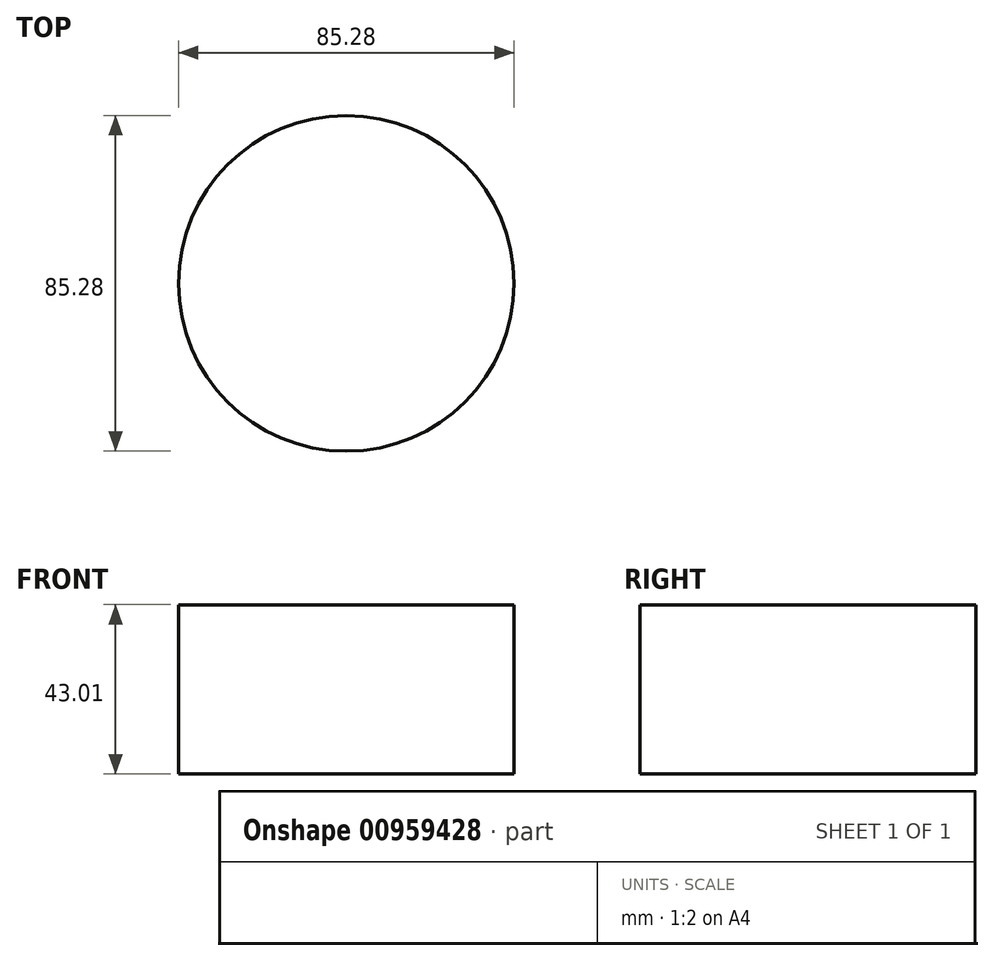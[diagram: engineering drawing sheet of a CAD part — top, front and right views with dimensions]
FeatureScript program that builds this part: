
annotation { "Feature Type Name" : "Feature", "Feature Type Description" : "" }
export const myFeature = defineFeature(function(context is Context, id is Id, definition is map)
    precondition{}
    {
        {
            var Q0;
            Q0=qCreatedBy(makeId("Front.planeOp"),FACE);
            var sketch = newSketch(context, id + "F0", { "sketchPlane" : qUnion([Q0])});
            skLineSegment(sketch, "E0", {"start": v(0, 0) * mm, "end": v(0, 43) * mm});
            skLineSegment(sketch, "E1", {"start": v(0, 43) * mm, "end": v(42.64, 43) * mm});
            skLineSegment(sketch, "E2", {"start": v(42.64, 43) * mm, "end": v(42.64, 0) * mm});
            skLineSegment(sketch, "E3", {"start": v(42.64, 0) * mm, "end": v(0, 0) * mm});
            skSolve(sketch);
        }
        {
            var Q0;
            Q0 = qSketchRegion(id + "F0", true);
            var Q1;
            Q1=sQuery(id+"F0.wireOp",EDGE,"E0");
            revolve(context, id + "F1", {"surfaceOperationType" : NewSurfaceOperationType.NEW, "entities" : qUnion([Q0]), "axis" : qUnion([Q1]), "revolveType" : RevolveType.FULL});
        }
    });
